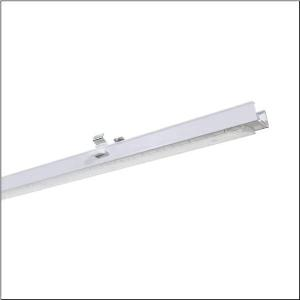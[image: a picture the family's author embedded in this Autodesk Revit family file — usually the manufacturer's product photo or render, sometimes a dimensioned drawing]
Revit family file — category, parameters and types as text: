
# Revit family: trunking_flex_31_51re12mb4cb
name_source: partatom
category: Lighting Fixtures
units: mm (PartAtom-declared; Revit-internal decimal feet)

## family parameters
Cut with Voids When Loaded = No
Host = Face
Light Source = No
Part Type = Normal
Room Calculation Point = No
Round Connector Dimension = Use Diameter
Shared = No

## types (1)
- --- (1 x LED, 11500 lm, 66 W, 4000K)
    Apparent Load = 66 VA
    CIE Flux Codes = 65 91 98 99 100
    Color Rendering = 80
    Color Temperature = 4000K
    Default Elevation = 1800 mm
    Description = Trunking Flex 31, luminaire insert, of extruded aluminium section, coated, traffic white (RAL 9016), length: 1.472mm, width: 91mm, height: 53mm, LED rated luminous flux: 11.500lm, light colour: 840, control gear: ON/OFF Multilumen, with system connector: socket, mains connection: 220..240V, AC, 50/60Hz, rated input power: 66W, connected load according to luminous flux setting (19/24/32/37/47/52/60/66W), luminous flux adjustable on luminaire in eight steps (3450/4380/5800/6700/8350/9200/10500/11500lm ), primary light control with lens, of plastic, primary optical cover: cover, of PMMA, light emission: direct distribution, protection rating (complete): IP20, insulation class (complete): insulation class I (protective earthing), certification: CE, UKCA, impact resistance: IK02, permissible ambient temperature for indoor applications: -20..+40°C, packaging unit: 1 piece
    Height = 58 mm
    Lamp = 1 x LED
    Lamp Light Flux = 11500 lm
    Lamp Power = 66 W
    Lamp count = 1
    Length = 1472 mm
    Luminous efficacy = 174 lm/W
    Manufacturer = Siteco
    ModVariant = No
    Model = 51RE12MB4CB
    Mounting Place = Ceiling
    Mounting Type = Pendant
    Number of Poles = 1
    OnlyDefault = Yes
    Power Factor = 1
    Product Name = Trunking Flex 31
    Product group = luminaire insert
    ProductGroupID = 901
    Protection Class = Protection class I
    Protection Degree = IP 20
    RLX_Detail_Level = 1
    RLX_Emergency_Light_Flux = 0 lm
    RLX_Emergency_Type = 0
    RLX_Emergency_Type_DB = No
    RlxData = <blob elided: 20969 chars, md5=e705cab4>
    Socket = socket
    Standby Power = 0 W
    System Light Flux = 11500 lm
    System Power = 66 W
    Type Comments = factory setting: luminous flux: 100 % | (ON | ON | ON)
    Type Image = l_1266702.jpg
    URL = http://relux.com
    VarID = @adj_001257
    Voltage = 0 V
    Weight = 0.00 kg
    Width = 65 mm

## geometry (parser evidence)
native form markers: Blend x4, Sweep x13
no freeform markers — native parametric forms only
